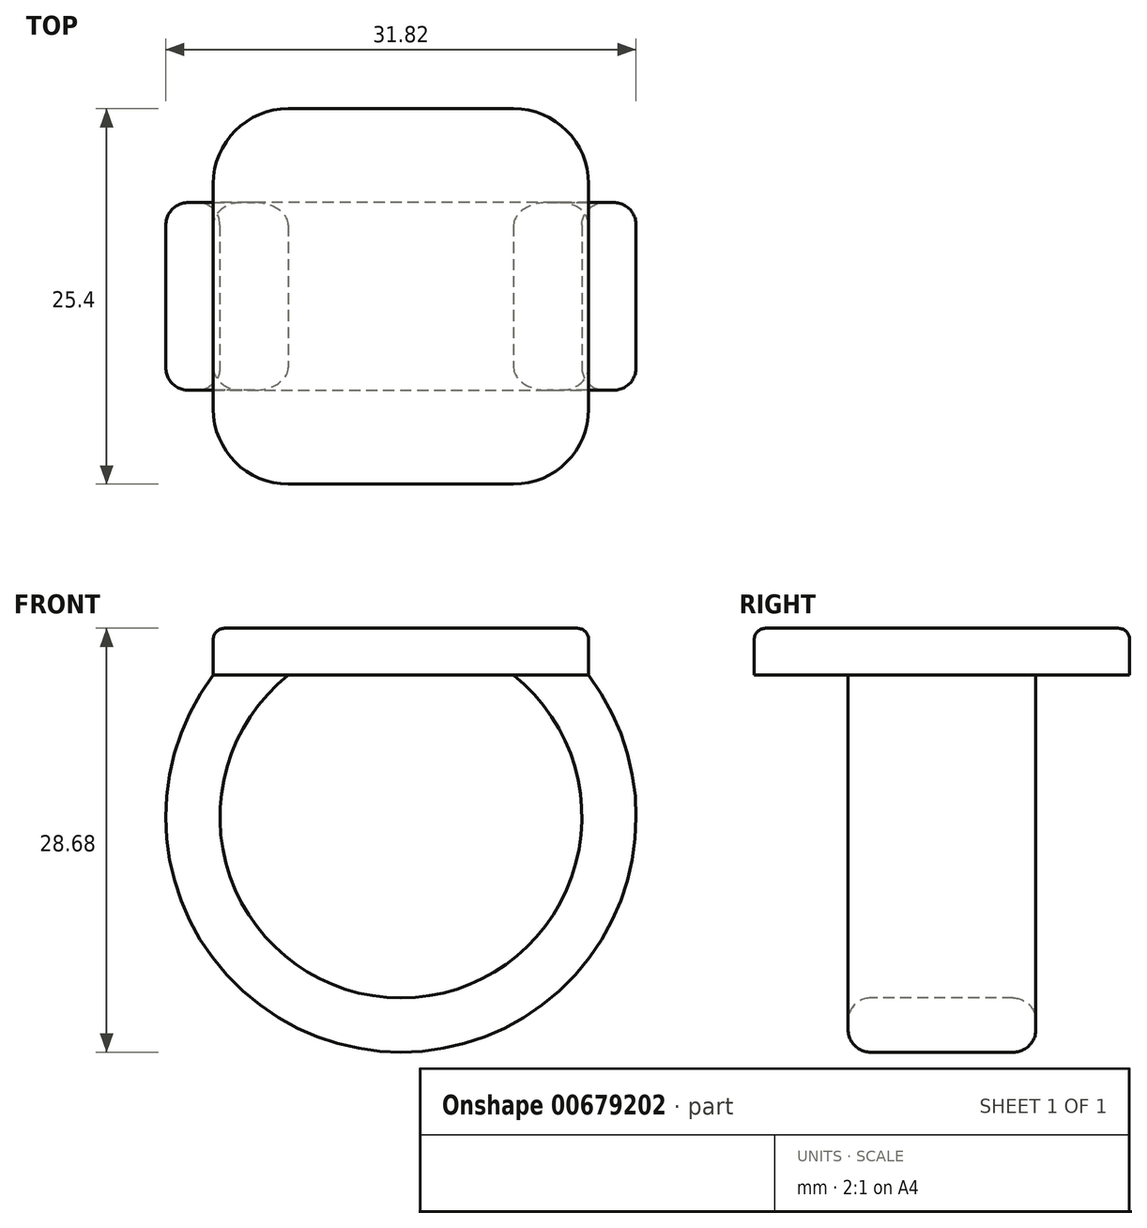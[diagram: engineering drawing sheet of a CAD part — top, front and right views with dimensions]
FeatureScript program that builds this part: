
annotation { "Feature Type Name" : "Feature", "Feature Type Description" : "" }
export const myFeature = defineFeature(function(context is Context, id is Id, definition is map)
    precondition{}
    {
        {
            var Q0;
            Q0=qCreatedBy(makeId("Top.planeOp"),FACE);
            var sketch = newSketch(context, id + "F0", { "sketchPlane" : qUnion([Q0])});
            skLineSegment(sketch, "E0.bottom", {"start": v(12.7, 12.7) * mm, "end": v(-12.7, 12.7) * mm});
            skLineSegment(sketch, "E0.top", {"start": v(12.7, -12.7) * mm, "end": v(-12.7, -12.7) * mm});
            skLineSegment(sketch, "E0.left", {"start": v(12.7, 12.7) * mm, "end": v(12.7, -12.7) * mm});
            skLineSegment(sketch, "E0.right", {"start": v(-12.7, 12.7) * mm, "end": v(-12.7, -12.7) * mm});
            skPoint(sketch, "E0.middle", {"position": v(0, 0) * mm});
            skSolve(sketch);
        }
        {
            var Q0;
            Q0 = qSketchRegion(id + "F0", true);
            extrude(context, id + "F1", {"entities" : qUnion([Q0]), "depth" : 3.17 * mm, "offsetDistance" : 25.4 * mm});
        }
        {
            var Q0;
            Q0=qCreatedBy(makeId("Front.planeOp"),FACE);
            var sketch = newSketch(context, id + "F2", { "sketchPlane" : qUnion([Q0])});
            skArc(sketch, "E1", {"start": v(-10.16, 0) * mm, "mid": v(0, -23.56) * mm, "end": v(10.16, 0) * mm});
            skSolve(sketch);
        }
        {
            var Q0;
            Q0=makeQuery(id+"F1.opExtrude","CAP_FACE",FACE,{"disambiguationData":[OSD([sQuery(id+"F0.wireOp",EDGE,"E0.bottom"),sQuery(id+"F0.wireOp",EDGE,"E0.top"),sQuery(id+"F0.wireOp",EDGE,"E0.left"),sQuery(id+"F0.wireOp",EDGE,"E0.right")])],"isStart":true});
            var sketch = newSketch(context, id + "F3", { "sketchPlane" : qUnion([Q0])});
            skLineSegment(sketch, "E2.bottom", {"start": v(-7.62, -6.35) * mm, "end": v(-12.7, -6.35) * mm});
            skLineSegment(sketch, "E2.top", {"start": v(-7.62, 6.35) * mm, "end": v(-12.7, 6.35) * mm});
            skLineSegment(sketch, "E2.left", {"start": v(-7.62, -6.35) * mm, "end": v(-7.62, 6.35) * mm});
            skLineSegment(sketch, "E2.right", {"start": v(-12.7, -6.35) * mm, "end": v(-12.7, 6.35) * mm});
            skPoint(sketch, "E2.middle", {"position": v(-10.16, 0) * mm});
            skSolve(sketch);
        }
        {
            var Q0;
            Q0 = qSketchRegion(id + "F3", true);
            var Q1;
            Q1 = qConstructionFilter(qBodyType(qCreatedBy(id + "F2" ,EDGE), BodyType.WIRE), ConstructionObject.NO);
            sweep(context, id + "F4", {"operationType" : NewBodyOperationType.ADD, "profiles" : qUnion([Q0]), "path" : qUnion([Q1])});
        }
        {
            var Q0;
            Q0=qCreatedBy(makeId("Front.planeOp"),FACE);
            var sketch = newSketch(context, id + "F5", { "sketchPlane" : qUnion([Q0])});
            skLineSegment(sketch, "E3.0", {"start": v(10.16, 0) * mm, "end": v(-7.62, 0) * mm});
            skLineSegment(sketch, "E3.1", {"start": v(10.01, -2.54) * mm, "end": v(10.16, 0) * mm});
            skArc(sketch, "E3.2", {"start": v(-7.62, 0) * mm, "mid": v(0, -21.84) * mm, "end": v(7.62, 0) * mm});
            skPoint(sketch, "E4.orphan", {"position": v(12.7, 0) * mm});
            skPoint(sketch, "E5.orphan", {"position": v(-12.7, 0) * mm});
            skSolve(sketch);
        }
        {
            var Q0;
            {var subQ0=sQuery(id+"F5.wireOp",EDGE,"E3.1");Q0=makeQuery(id+"F5.imprint","IMPRINT",FACE,{"disambiguationData":[TD([[makeQuery(id+"F5.imprint","IMPRINT",EDGE,{"derivedFrom":subQ0}),1.0]])]});}
            var Q1;
            Q1=makeQuery(id+"F4.opSweep","SWEPT_FACE",FACE,{"disambiguationData":[OSD([sQuery(id+"F2.wireOp",EDGE,"E1"),sQuery(id+"F3.wireOp",EDGE,"E2.bottom")])]});
            extrude(context, id + "F6", {"entities" : qUnion([Q0]), "operationType" : NewBodyOperationType.ADD, "endBound" : BoundingType.UP_TO_SURFACE, "oppositeDirection" : true, "depth" : 25.4 * mm, "endBoundEntityFace" : qUnion([Q1]), "offsetDistance" : 25.4 * mm});
        }
        {
            var Q0;
            Q0=makeQuery(id+"F6.opExtrude","CAP_FACE",FACE,{"disambiguationData":[OSD([sQuery(id+"F5.wireOp",EDGE,"E3.0"),sQuery(id+"F5.wireOp",EDGE,"E3.1"),sQuery(id+"F5.wireOp",EDGE,"E3.2")])],"isStart":true});
            var Q1;
            Q1=makeQuery(id+"F4.opSweep","SWEPT_FACE",FACE,{"disambiguationData":[OSD([sQuery(id+"F2.wireOp",EDGE,"E1"),sQuery(id+"F3.wireOp",EDGE,"E2.top")])]});
            extrude(context, id + "F7", {"entities" : qUnion([Q0]), "operationType" : NewBodyOperationType.ADD, "endBound" : BoundingType.UP_TO_SURFACE, "depth" : 25.4 * mm, "endBoundEntityFace" : qUnion([Q1]), "offsetDistance" : 25.4 * mm});
        }
        {
            var Q0;
            Q0=makeQuery(id+"F1.opExtrude","SWEPT_EDGE",EDGE,{"disambiguationData":[OSD([sQuery(id+"F0.wireOp",EDGE,"E0.top"),sQuery(id+"F0.wireOp",EDGE,"E0.left")])]});
            var Q1;
            Q1=makeQuery(id+"F1.opExtrude","SWEPT_EDGE",EDGE,{"disambiguationData":[OSD([sQuery(id+"F0.wireOp",EDGE,"E0.bottom"),sQuery(id+"F0.wireOp",EDGE,"E0.left")])]});
            var Q2;
            Q2=makeQuery(id+"F1.opExtrude","SWEPT_EDGE",EDGE,{"disambiguationData":[OSD([sQuery(id+"F0.wireOp",EDGE,"E0.bottom"),sQuery(id+"F0.wireOp",EDGE,"E0.right")])]});
            var Q3;
            Q3=makeQuery(id+"F1.opExtrude","SWEPT_EDGE",EDGE,{"disambiguationData":[OSD([sQuery(id+"F0.wireOp",EDGE,"E0.top"),sQuery(id+"F0.wireOp",EDGE,"E0.right")])]});
            fillet(context, id + "F8", {"entities" : qUnion([Q0, Q1, Q2, Q3]), "radius" : 5.08 * mm, "tangentPropagation" : true, "allowEdgeOverflow" : false});
        }
        {
            var Q0;
            Q0=makeQuery(id+"F4.opSweep","SWEPT_EDGE",EDGE,{"disambiguationData":[OSD([sQuery(id+"F0.wireOp",EDGE,"E0.right"),sQuery(id+"F2.wireOp",EDGE,"E1"),sQuery(id+"F3.wireOp",EDGE,"E2.top"),sQuery(id+"F3.wireOp",EDGE,"E2.right")])]});
            var Q1;
            {var subQ0=sQuery(id+"F3.wireOp",EDGE,"E2.top");var subQ1=sQuery(id+"F2.wireOp",EDGE,"E1");Q1=makeQuery(id+"F7.boolean.opBoolean","MERGE",EDGE,{"derivedFrom":[makeQuery(id+"F4.opSweep","SWEPT_EDGE",EDGE,{"disambiguationData":[OSD([subQ1,subQ0,sQuery(id+"F3.wireOp",EDGE,"E2.left")])]}),makeQuery(id+"F7.opExtrude","TWEAK_EDGE",EDGE,{"derivedFrom":[makeQuery(id+"F4.opSweep","SWEPT_FACE",FACE,{"disambiguationData":[OSD([subQ1,subQ0])]}),makeQuery(id+"F6.opExtrude","CAP_EDGE",EDGE,{"disambiguationData":[OSD([sQuery(id+"F5.wireOp",EDGE,"E3.2")])],"isStart":true})]})]});}
            var Q2;
            {var subQ0=sQuery(id+"F5.wireOp",EDGE,"E3.2");var subQ1=sQuery(id+"F3.wireOp",EDGE,"E2.bottom");var subQ2=sQuery(id+"F2.wireOp",EDGE,"E1");Q2=makeQuery(id+"F6.boolean.opBoolean","MERGE",EDGE,{"derivedFrom":[makeQuery(id+"F4.opSweep","SWEPT_EDGE",EDGE,{"disambiguationData":[OSD([subQ2,subQ1,sQuery(id+"F3.wireOp",EDGE,"E2.left")])]}),makeQuery(id+"F6.opExtrude","TWEAK_EDGE",EDGE,{"derivedFrom":[makeQuery(id+"F4.opSweep","SWEPT_FACE",FACE,{"disambiguationData":[OSD([subQ2,subQ1])]}),makeQuery(id+"F5.imprint","IMPRINT",EDGE,{"disambiguationData":[TD([[makeQuery(id+"F5.imprint","INTERSECT",VERTEX,{"derivedFrom":[sQuery(id+"F5.wireOp",EDGE,"E3.1"),subQ0]}),-1.0]])],"derivedFrom":subQ0})]})]});}
            var Q3;
            Q3=makeQuery(id+"F4.opSweep","SWEPT_EDGE",EDGE,{"disambiguationData":[OSD([sQuery(id+"F0.wireOp",EDGE,"E0.right"),sQuery(id+"F2.wireOp",EDGE,"E1"),sQuery(id+"F3.wireOp",EDGE,"E2.bottom"),sQuery(id+"F3.wireOp",EDGE,"E2.right")])]});
            fillet(context, id + "F9", {"entities" : qUnion([Q0, Q1, Q2, Q3]), "radius" : 1.52 * mm, "tangentPropagation" : true, "allowEdgeOverflow" : false});
        }
        {
            var Q0;
            Q0=makeQuery(id+"F1.opExtrude","CAP_FACE",FACE,{"disambiguationData":[OSD([sQuery(id+"F0.wireOp",EDGE,"E0.bottom"),sQuery(id+"F0.wireOp",EDGE,"E0.top"),sQuery(id+"F0.wireOp",EDGE,"E0.left"),sQuery(id+"F0.wireOp",EDGE,"E0.right")])],"isStart":false});
            fillet(context, id + "F10", {"entities" : qUnion([Q0]), "radius" : 0.76 * mm, "tangentPropagation" : true, "allowEdgeOverflow" : false});
        }
    });
